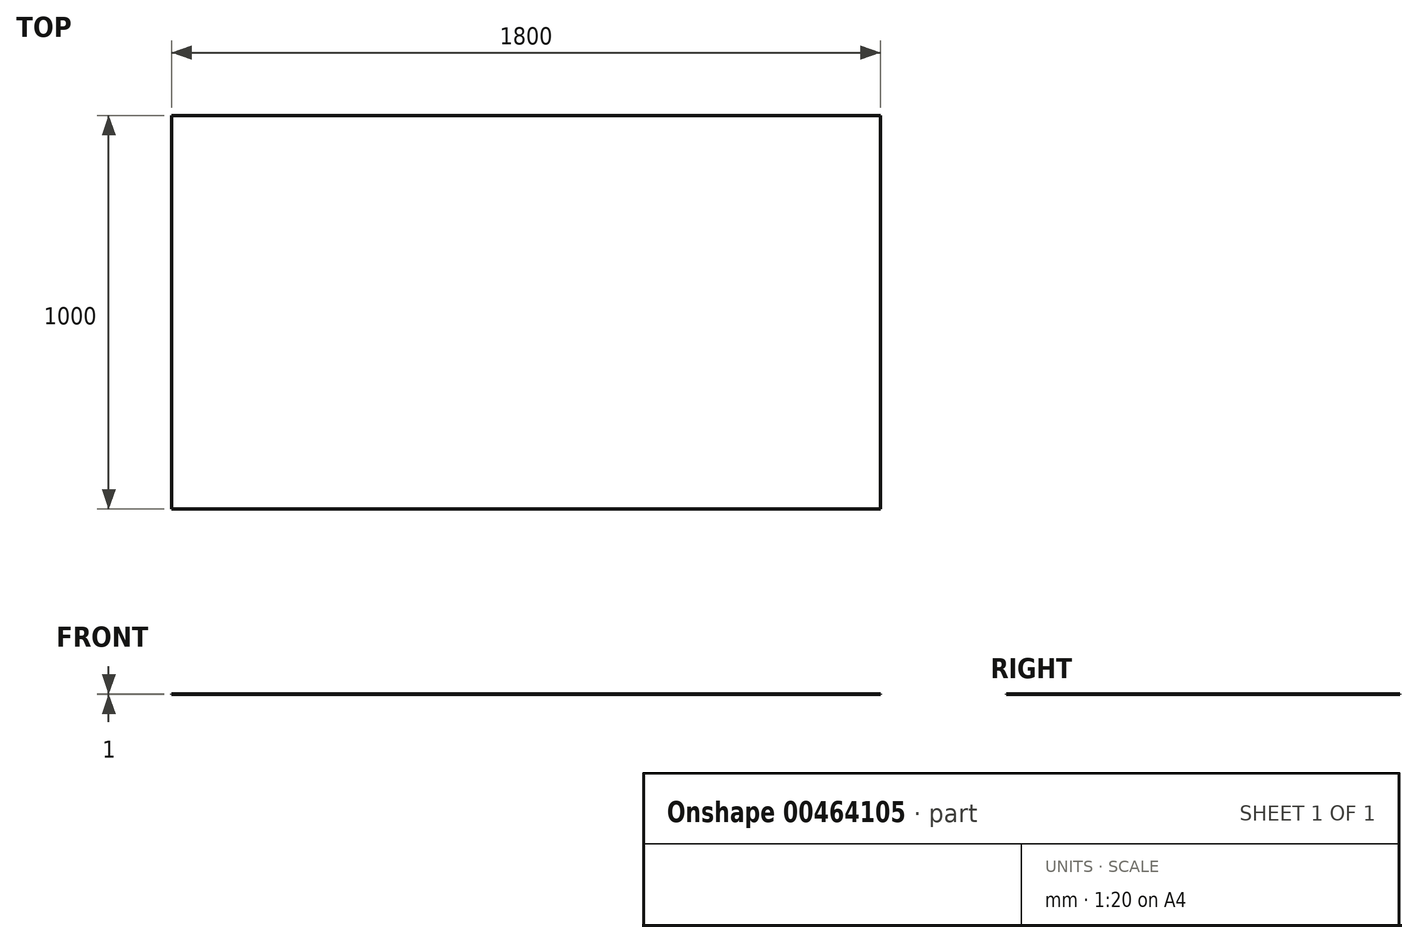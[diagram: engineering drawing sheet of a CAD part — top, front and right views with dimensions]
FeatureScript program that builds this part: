
annotation { "Feature Type Name" : "Feature", "Feature Type Description" : "" }
export const myFeature = defineFeature(function(context is Context, id is Id, definition is map)
    precondition{}
    {
        {
            var Q0;
            Q0=qCreatedBy(makeId("Top.planeOp"),FACE);
            var sketch = newSketch(context, id + "F0", { "sketchPlane" : qUnion([Q0])});
            skLineSegment(sketch, "E0.bottom", {"start": v(0, 0) * mm, "end": v(-1800, 0) * mm});
            skLineSegment(sketch, "E0.top", {"start": v(0, -1000) * mm, "end": v(-1800, -1000) * mm});
            skLineSegment(sketch, "E0.left", {"start": v(0, 0) * mm, "end": v(0, -1000) * mm});
            skLineSegment(sketch, "E0.right", {"start": v(-1800, 0) * mm, "end": v(-1800, -1000) * mm});
            skSolve(sketch);
        }
        {
            var Q0;
            Q0=qSketchRegion(id+"F0",true);
            extrude(context, id + "F1", {"entities" : qUnion([Q0]), "depth" : 1 * mm});
        }
    });
